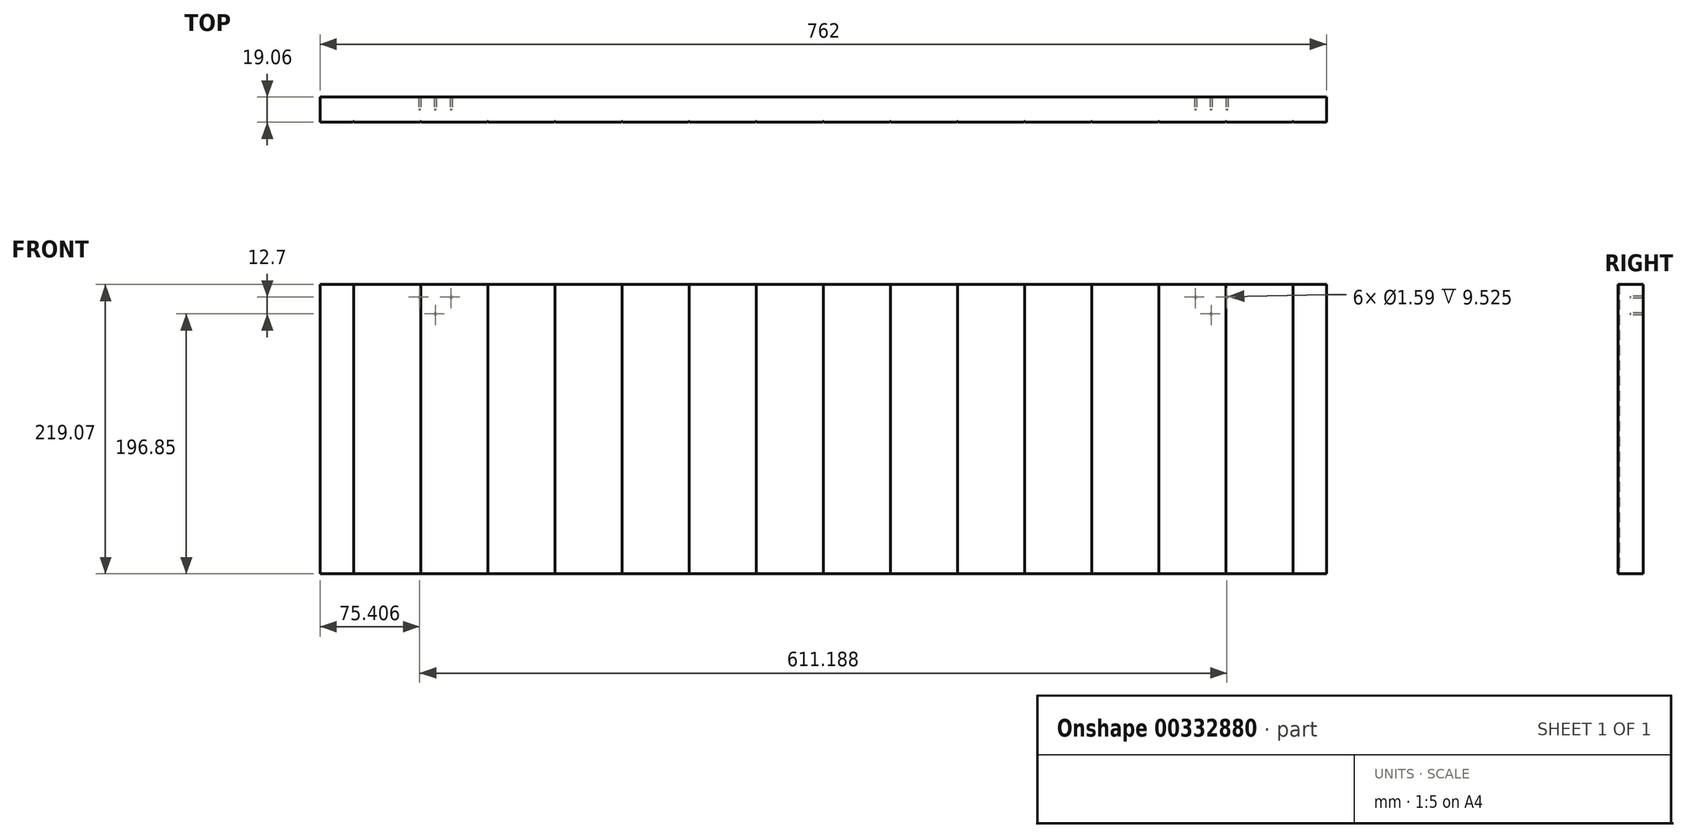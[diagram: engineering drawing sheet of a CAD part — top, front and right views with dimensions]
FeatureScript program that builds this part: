
annotation { "Feature Type Name" : "Feature", "Feature Type Description" : "" }
export const myFeature = defineFeature(function(context is Context, id is Id, definition is map)
    precondition{}
    {
        {
            var Q0;
            Q0=qCreatedBy(makeId("Top.planeOp"),FACE);
            var sketch = newSketch(context, id + "F0", { "sketchPlane" : qUnion([Q0])});
            skLineSegment(sketch, "E0.bottom", {"start": v(508, -9.53) * mm, "end": v(458.22, -9.53) * mm});
            skLineSegment(sketch, "E0.top", {"start": v(508, 9.53) * mm, "end": v(-508, 9.53) * mm});
            skLineSegment(sketch, "E0.left", {"start": v(508, 9.53) * mm, "end": v(508, -9.53) * mm});
            skLineSegment(sketch, "E0.right", {"start": v(-508, 9.53) * mm, "end": v(-508, -9.53) * mm});
            skPoint(sketch, "E0.middle", {"position": v(0, 0) * mm});
            skArc(sketch, "E1", {"start": v(-509.02, -9.53) * mm, "mid": v(-508.3, -9.23) * mm, "end": v(-508, -8.5) * mm});
            skArc(sketch, "E2", {"start": v(-508, -8.5) * mm, "mid": v(-507.7, -9.23) * mm, "end": v(-506.98, -9.52) * mm});
            skArc(sketch, "E3.1.0.0", {"start": v(-458.22, -9.53) * mm, "mid": v(-457.5, -9.23) * mm, "end": v(-457.2, -8.5) * mm});
            skArc(sketch, "E3.1.0.1", {"start": v(-457.2, -8.5) * mm, "mid": v(-456.9, -9.23) * mm, "end": v(-456.18, -9.52) * mm});
            skArc(sketch, "E3.2.0.0", {"start": v(-407.42, -9.53) * mm, "mid": v(-406.7, -9.23) * mm, "end": v(-406.4, -8.5) * mm});
            skArc(sketch, "E3.2.0.1", {"start": v(-406.4, -8.5) * mm, "mid": v(-406.1, -9.23) * mm, "end": v(-405.38, -9.52) * mm});
            skArc(sketch, "E3.3.0.0", {"start": v(-356.62, -9.53) * mm, "mid": v(-355.9, -9.23) * mm, "end": v(-355.6, -8.5) * mm});
            skArc(sketch, "E3.3.0.1", {"start": v(-355.6, -8.5) * mm, "mid": v(-355.3, -9.23) * mm, "end": v(-354.58, -9.52) * mm});
            skArc(sketch, "E3.4.0.0", {"start": v(-305.82, -9.53) * mm, "mid": v(-305.1, -9.23) * mm, "end": v(-304.8, -8.5) * mm});
            skArc(sketch, "E3.4.0.1", {"start": v(-304.8, -8.5) * mm, "mid": v(-304.5, -9.23) * mm, "end": v(-303.78, -9.52) * mm});
            skArc(sketch, "E3.5.0.0", {"start": v(-255.02, -9.53) * mm, "mid": v(-254.3, -9.23) * mm, "end": v(-254, -8.5) * mm});
            skArc(sketch, "E3.5.0.1", {"start": v(-254, -8.5) * mm, "mid": v(-253.7, -9.23) * mm, "end": v(-252.98, -9.52) * mm});
            skArc(sketch, "E3.6.0.0", {"start": v(-204.22, -9.53) * mm, "mid": v(-203.5, -9.23) * mm, "end": v(-203.2, -8.5) * mm});
            skArc(sketch, "E3.6.0.1", {"start": v(-203.2, -8.5) * mm, "mid": v(-202.9, -9.23) * mm, "end": v(-202.18, -9.52) * mm});
            skArc(sketch, "E3.7.0.0", {"start": v(-153.42, -9.53) * mm, "mid": v(-152.7, -9.23) * mm, "end": v(-152.4, -8.5) * mm});
            skArc(sketch, "E3.7.0.1", {"start": v(-152.4, -8.5) * mm, "mid": v(-152.1, -9.23) * mm, "end": v(-151.38, -9.52) * mm});
            skArc(sketch, "E3.8.0.0", {"start": v(-102.62, -9.53) * mm, "mid": v(-101.9, -9.23) * mm, "end": v(-101.6, -8.5) * mm});
            skArc(sketch, "E3.8.0.1", {"start": v(-101.6, -8.5) * mm, "mid": v(-101.3, -9.23) * mm, "end": v(-100.58, -9.52) * mm});
            skArc(sketch, "E3.9.0.0", {"start": v(-51.82, -9.53) * mm, "mid": v(-51.1, -9.23) * mm, "end": v(-50.8, -8.5) * mm});
            skArc(sketch, "E3.9.0.1", {"start": v(-50.8, -8.5) * mm, "mid": v(-50.5, -9.23) * mm, "end": v(-49.78, -9.52) * mm});
            skArc(sketch, "E3.10.0.0", {"start": v(-1.02, -9.53) * mm, "mid": v(-0.3, -9.23) * mm, "end": v(0, -8.5) * mm});
            skArc(sketch, "E3.10.0.1", {"start": v(0, -8.5) * mm, "mid": v(0.3, -9.23) * mm, "end": v(1.02, -9.52) * mm});
            skArc(sketch, "E3.11.0.0", {"start": v(49.78, -9.53) * mm, "mid": v(50.5, -9.23) * mm, "end": v(50.8, -8.5) * mm});
            skArc(sketch, "E3.11.0.1", {"start": v(50.8, -8.5) * mm, "mid": v(51.1, -9.23) * mm, "end": v(51.82, -9.52) * mm});
            skArc(sketch, "E3.12.0.0", {"start": v(100.58, -9.53) * mm, "mid": v(101.3, -9.23) * mm, "end": v(101.6, -8.5) * mm});
            skArc(sketch, "E3.12.0.1", {"start": v(101.6, -8.5) * mm, "mid": v(101.9, -9.23) * mm, "end": v(102.62, -9.52) * mm});
            skArc(sketch, "E3.13.0.0", {"start": v(151.38, -9.53) * mm, "mid": v(152.1, -9.23) * mm, "end": v(152.4, -8.5) * mm});
            skArc(sketch, "E3.13.0.1", {"start": v(152.4, -8.5) * mm, "mid": v(152.7, -9.23) * mm, "end": v(153.42, -9.52) * mm});
            skArc(sketch, "E3.14.0.0", {"start": v(202.18, -9.53) * mm, "mid": v(202.9, -9.23) * mm, "end": v(203.2, -8.5) * mm});
            skArc(sketch, "E3.14.0.1", {"start": v(203.2, -8.5) * mm, "mid": v(203.5, -9.23) * mm, "end": v(204.22, -9.52) * mm});
            skArc(sketch, "E3.15.0.0", {"start": v(252.98, -9.53) * mm, "mid": v(253.7, -9.23) * mm, "end": v(254, -8.5) * mm});
            skArc(sketch, "E3.15.0.1", {"start": v(254, -8.5) * mm, "mid": v(254.3, -9.23) * mm, "end": v(255.02, -9.52) * mm});
            skArc(sketch, "E3.16.0.0", {"start": v(303.78, -9.53) * mm, "mid": v(304.5, -9.23) * mm, "end": v(304.8, -8.5) * mm});
            skArc(sketch, "E3.16.0.1", {"start": v(304.8, -8.5) * mm, "mid": v(305.1, -9.23) * mm, "end": v(305.82, -9.52) * mm});
            skArc(sketch, "E3.17.0.0", {"start": v(354.58, -9.53) * mm, "mid": v(355.3, -9.23) * mm, "end": v(355.6, -8.5) * mm});
            skArc(sketch, "E3.17.0.1", {"start": v(355.6, -8.5) * mm, "mid": v(355.9, -9.23) * mm, "end": v(356.62, -9.52) * mm});
            skArc(sketch, "E3.18.0.0", {"start": v(405.38, -9.53) * mm, "mid": v(406.1, -9.23) * mm, "end": v(406.4, -8.5) * mm});
            skArc(sketch, "E3.18.0.1", {"start": v(406.4, -8.5) * mm, "mid": v(406.7, -9.23) * mm, "end": v(407.42, -9.52) * mm});
            skArc(sketch, "E3.19.0.0", {"start": v(456.18, -9.53) * mm, "mid": v(456.9, -9.23) * mm, "end": v(457.2, -8.5) * mm});
            skArc(sketch, "E3.19.0.1", {"start": v(457.2, -8.5) * mm, "mid": v(457.5, -9.23) * mm, "end": v(458.22, -9.52) * mm});
            skLineSegment(sketch, "E3.direction1", {"start": v(-506.98, -9.53) * mm, "end": v(-458.22, -9.53) * mm, "construction": true});
            skLineSegment(sketch, "E4.trimOffspring", {"start": v(-458.22, -9.53) * mm, "end": v(-508, -9.53) * mm});
            skLineSegment(sketch, "E5.trimOffspring", {"start": v(-407.42, -9.53) * mm, "end": v(-456.18, -9.53) * mm});
            skLineSegment(sketch, "E6.trimOffspring", {"start": v(-356.62, -9.53) * mm, "end": v(-405.38, -9.53) * mm});
            skLineSegment(sketch, "E7.trimOffspring", {"start": v(-305.82, -9.53) * mm, "end": v(-354.58, -9.53) * mm});
            skLineSegment(sketch, "E8.trimOffspring", {"start": v(-255.02, -9.53) * mm, "end": v(-303.78, -9.53) * mm});
            skLineSegment(sketch, "E9.trimOffspring", {"start": v(-204.22, -9.53) * mm, "end": v(-252.98, -9.53) * mm});
            skLineSegment(sketch, "E10.trimOffspring", {"start": v(-153.42, -9.53) * mm, "end": v(-202.18, -9.53) * mm});
            skLineSegment(sketch, "E11.trimOffspring", {"start": v(-102.62, -9.53) * mm, "end": v(-151.38, -9.53) * mm});
            skLineSegment(sketch, "E12.trimOffspring", {"start": v(-51.82, -9.53) * mm, "end": v(-100.58, -9.53) * mm});
            skLineSegment(sketch, "E13.trimOffspring", {"start": v(-1.02, -9.53) * mm, "end": v(-49.78, -9.53) * mm});
            skLineSegment(sketch, "E14.trimOffspring", {"start": v(49.78, -9.53) * mm, "end": v(1.02, -9.53) * mm});
            skLineSegment(sketch, "E15.trimOffspring", {"start": v(100.58, -9.53) * mm, "end": v(51.82, -9.53) * mm});
            skLineSegment(sketch, "E16.trimOffspring", {"start": v(151.38, -9.53) * mm, "end": v(102.62, -9.53) * mm});
            skLineSegment(sketch, "E17.trimOffspring", {"start": v(202.18, -9.53) * mm, "end": v(153.42, -9.53) * mm});
            skLineSegment(sketch, "E18.trimOffspring", {"start": v(252.98, -9.53) * mm, "end": v(204.22, -9.53) * mm});
            skLineSegment(sketch, "E19.trimOffspring", {"start": v(303.78, -9.53) * mm, "end": v(255.02, -9.53) * mm});
            skLineSegment(sketch, "E20.trimOffspring", {"start": v(354.58, -9.53) * mm, "end": v(305.82, -9.53) * mm});
            skLineSegment(sketch, "E21.trimOffspring", {"start": v(405.38, -9.53) * mm, "end": v(356.62, -9.53) * mm});
            skLineSegment(sketch, "E22.trimOffspring", {"start": v(456.18, -9.53) * mm, "end": v(407.42, -9.53) * mm});
            skSolve(sketch);
        }
        {
            var Q0;
            Q0=qSketchRegion(id+"F0",true);
            extrude(context, id + "F1", {"entities" : qUnion([Q0]), "depth" : 219.07 * mm});
        }
        {
            var Q0;
            Q0=qCreatedBy(makeId("Top.planeOp"),FACE);
            var sketch = newSketch(context, id + "F2", { "sketchPlane" : qUnion([Q0])});
            skLineSegment(sketch, "E23.bottom", {"start": v(381, -89.59) * mm, "end": v(724.07, -89.59) * mm});
            skLineSegment(sketch, "E23.top", {"start": v(381, 47.64) * mm, "end": v(724.07, 47.64) * mm});
            skLineSegment(sketch, "E23.left", {"start": v(381, -89.59) * mm, "end": v(381, 47.64) * mm});
            skLineSegment(sketch, "E23.right", {"start": v(724.07, -89.59) * mm, "end": v(724.07, 47.64) * mm});
            skLineSegment(sketch, "E24.bottom", {"start": v(-381, -137.09) * mm, "end": v(-685.36, -137.09) * mm});
            skLineSegment(sketch, "E24.top", {"start": v(-381, 58.2) * mm, "end": v(-685.36, 58.2) * mm});
            skLineSegment(sketch, "E24.left", {"start": v(-381, -137.09) * mm, "end": v(-381, 58.2) * mm});
            skLineSegment(sketch, "E24.right", {"start": v(-685.36, -137.09) * mm, "end": v(-685.36, 58.2) * mm});
            skSolve(sketch);
        }
        {
            var Q0;
            Q0 = qSketchRegion(id + "F2", true);
            extrude(context, id + "F3", {"entities" : qUnion([Q0]), "operationType" : NewBodyOperationType.REMOVE, "depth" : 1143 * mm});
        }
        {
            var Q0;
            Q0=qCreatedBy(makeId("Front.planeOp"),FACE);
            var sketch = newSketch(context, id + "F4", { "sketchPlane" : qUnion([Q0])});
            skLineSegment(sketch, "E25", {"start": v(381, 209.55) * mm, "end": v(-381, 209.55) * mm, "construction": true});
            skLineSegment(sketch, "E26.bottom", {"start": v(381, 266.12) * mm, "end": v(-381, 266.12) * mm, "construction": true});
            skLineSegment(sketch, "E26.top", {"start": v(381, 152.98) * mm, "end": v(-381, 152.98) * mm, "construction": true});
            skLineSegment(sketch, "E26.left", {"start": v(381, 266.12) * mm, "end": v(381, 152.98) * mm, "construction": true});
            skLineSegment(sketch, "E26.right", {"start": v(-381, 266.12) * mm, "end": v(-381, 152.98) * mm, "construction": true});
            skPoint(sketch, "E26.middle", {"position": v(0, 209.55) * mm});
            skLineSegment(sketch, "E27", {"start": v(-293.69, 266.12) * mm, "end": v(-293.69, 152.98) * mm, "construction": true});
            skLineSegment(sketch, "E28", {"start": v(-293.69, 196.85) * mm, "end": v(293.69, 196.85) * mm, "construction": true});
            skLineSegment(sketch, "E29", {"start": v(293.69, 266.12) * mm, "end": v(293.69, 152.98) * mm, "construction": true});
            skCircle(sketch, "E30", {"center": v(-293.69, 196.85) * mm, "radius": 0.8 * mm});
            skCircle(sketch, "E31", {"center": v(-281.78, 209.55) * mm, "radius": 0.8 * mm});
            skCircle(sketch, "E32", {"center": v(-305.6, 209.55) * mm, "radius": 0.8 * mm});
            skCircle(sketch, "E33", {"center": v(293.69, 196.85) * mm, "radius": 0.8 * mm});
            skCircle(sketch, "E34", {"center": v(305.6, 209.55) * mm, "radius": 0.8 * mm});
            skCircle(sketch, "E35", {"center": v(281.78, 209.55) * mm, "radius": 0.8 * mm});
            skSolve(sketch);
        }
        {
            var Q0;
            Q0 = qSketchRegion(id + "F4", true);
            extrude(context, id + "F5", {"entities" : qUnion([Q0]), "operationType" : NewBodyOperationType.REMOVE, "oppositeDirection" : true, "depth" : 25.4 * mm});
        }
    });
